# Revit family: Deployable-Draft-Curtain_DoorSystems
name_source: partatom
category: Specialty Equipment
units: mm (PartAtom-declared; Revit-internal decimal feet)

## family parameters
Always vertical = No
Cut with Voids When Loaded = No
Enable Cutting in Views = No
Maintain Annotation Orientation = No
OmniClass Number = 23.30.60.17
OmniClass Title = Fire and Smoke Shutters and Curtains
Part Type = Normal
Room Calculation Point = No
Round Connector Dimension = Use Diameter
Shared = No
Work Plane-Based = Yes

## types (3) — shared parameters
Assembly Code = D4090
Construction Details = http://www.arcat.com
Default Elevation = 0' - 0"
Electrical_Voltage = 24 V
Fire Performance = Fire Rating as Specified  ;  UL10B and UL 263 Time Curve
Keynote = 08 34 85
Manufacturer = Door Systems, Inc
Manufacturer Website = http://www.doorsysinc.com
Maximum Size = 14 ft Wide. Heights Above 10 ft Require Larger Head Clearances
Model = as Specified
Product Data = http://www.arcat.com
Product Properties = http://www.doorsysinc.com
Sales Information = http://www.doorsysinc.com
Specification = http://www.arcat.com
Standards Conformance = IBC 715.4 C  ;  NFPA 101 and 105  ;  UL 1784 S Label  ;  UL 864  ;  UL 555
URL = http://www.doorsysinc.com
zero-valued in all types: Expected Lifespan (Years), Maintenance Schedule (Months), Warranty Duration (Years)

## per-type parameters (varying)
| type | Description | Revision |
| Multiple Roller Over Under | Door Systems Inc Fire Rated Smoke Curtain - as Specified | R1_2016-07 |
| Multiple Roller Side by Side | Door Systems Inc Fire Rated Smoke Curtain - as Specified | R1_2016-07 |
| Single Roller | Door Systems Inc Draft Curtain - as Specified |  |

type visibility flags (boolean, named after types; folded from table):
- Multiple Roller Over Under: Yes: Multiple Roller Over Under
- Multiple Roller Side by Side: Yes: Multiple Roller Side by Side
- Single Roller: Yes: (none)

## geometry (parser evidence)
native form markers: Sweep x3
no freeform markers — native parametric forms only
